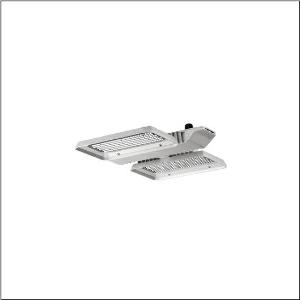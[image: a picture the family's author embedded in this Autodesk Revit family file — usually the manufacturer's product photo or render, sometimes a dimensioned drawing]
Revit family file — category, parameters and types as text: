
# Revit family: highbay_11_51hla2d14fcad
name_source: partatom
category: Lighting Fixtures
units: mm (PartAtom-declared; Revit-internal decimal feet)

## family parameters
Cut with Voids When Loaded = No
Host = Face
Light Source = No
Part Type = Normal
Room Calculation Point = No
Round Connector Dimension = Use Diameter
Shared = No

## types (1)
- --- (1 x LED, 2160 lm, 14 W, 4000K)
    Apparent Load = 14 VA
    CIE Flux Codes = 89 96 99 100 100
    Color Rendering = 80
    Color Temperature = 4000K
    Default Elevation = 1800 mm
    Description = Highbay 11, LED high bay luminaire, primary light control with lens, of PMMA, light emission: direct distribution, primary light characteristic: symmetric, installation type: suspended mounting, surface-mounted, for 1x 2x LED, rated luminous flux: 14.400lm, luminous efficacy: 177lm/W, light colour: 840, colour temperature: 4000K, control gear: ECG DALI, with terminal, 5-pole, max. 2.5mm², mains connection: 230..240V, AC/DC, 50/60Hz, rated input power: 81W, LED unit, of diecast aluminium, bead blasted, unplated, silver, length: 470mm, width: 500mm, height: 65mm, housing, of diecast aluminium, bead blasted, uncoated, silver, protection rating (complete): IP65, insulation class (complete): insulation class I (protective earthing), certification: CE, UKCA, protection symbol: D, impact resistance: IK08 with glass or PC cover, permissible operating ambient temperature: -35..+55°C, standard: EN 60598-2-22, reducing of maximum allowable ambient temperature of 5°C with ceiling mounting, corresponds to IFS (International Featured Standards) requirements for safety and quality in the food industry, packaging unit: 1 piece
    Height = 95 mm
    Lamp = 1 x LED
    Lamp Light Flux = 2160 lm
    Lamp Power = 14 W
    Lamp count = 1
    Length = 468 mm
    Luminous efficacy = 154 lm/W
    Manufacturer = Siteco
    ModVariant = No
    Model = 51HLA2D14FCAD
    Mounting Place = Ceiling
    Mounting Type = Pendant
    Number of Poles = 1
    OnlyDefault = Yes
    Power Factor = 1
    Product Name = Highbay 11
    Product group = LED high bay luminaire
    ProductGroupID = 903
    Protection Class = Protection class I
    Protection Degree = IP 65
    RLX_Detail_Level = 1
    RLX_Emergency_Light_Flux = 0 lm
    RLX_Emergency_Type = 0
    RLX_Emergency_Type_DB = No
    RlxData = <blob elided: 86441 chars, md5=72fb8a33>
    Socket = socket
    Standby Power = 0 W
    System Light Flux = 2160 lm
    System Power = 14 W
    Type Comments = : central accumulator DC – ECG emengency level 15%
    Type Image = l_1003425.jpg
    URL = http://relux.com
    VarID = @adj_152825
    Voltage = 0 V
    Weight = 0.00 kg
    Width = 501 mm

## geometry (parser evidence)
native form markers: Blend x4, Sweep x12
no freeform markers — native parametric forms only
